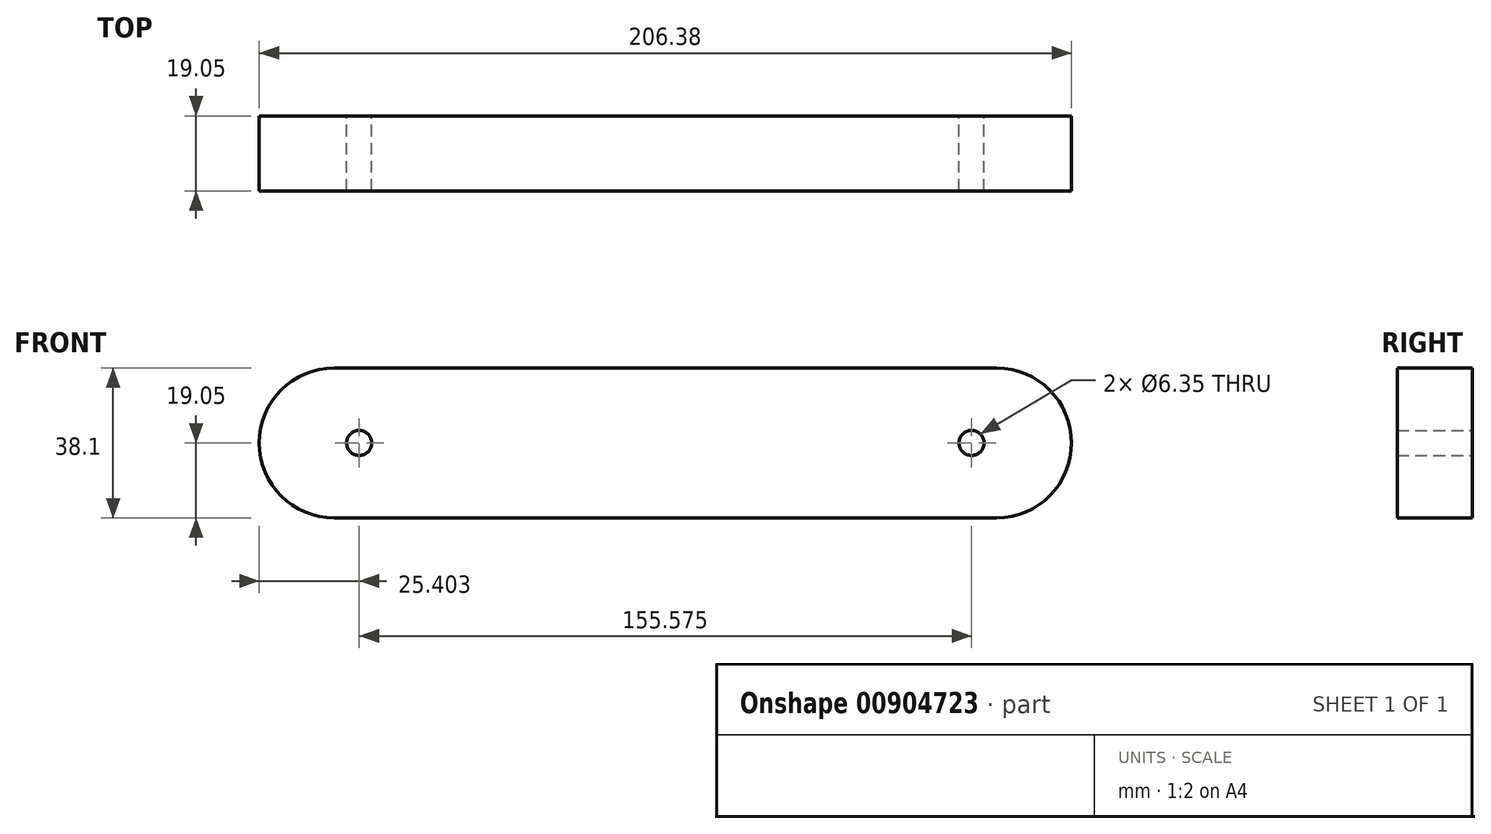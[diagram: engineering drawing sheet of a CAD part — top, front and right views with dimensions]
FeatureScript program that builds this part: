
annotation { "Feature Type Name" : "Feature", "Feature Type Description" : "" }
export const myFeature = defineFeature(function(context is Context, id is Id, definition is map)
    precondition{}
    {
        {
            var Q0;
            Q0=qCreatedBy(makeId("Front.planeOp"),FACE);
            var sketch = newSketch(context, id + "F0", { "sketchPlane" : qUnion([Q0])});
            skLineSegment(sketch, "E0.bottom", {"start": v(-84.14, -19.05) * mm, "end": v(84.14, -19.05) * mm});
            skLineSegment(sketch, "E0.top", {"start": v(-84.14, 19.05) * mm, "end": v(84.14, 19.05) * mm});
            skPoint(sketch, "E0.middle", {"position": v(0, 0) * mm});
            skArc(sketch, "E1", {"start": v(-84.14, 19.05) * mm, "mid": v(-103.19, 0) * mm, "end": v(-84.14, -19.05) * mm});
            skArc(sketch, "E2", {"start": v(84.14, 19.05) * mm, "mid": v(103.19, 0) * mm, "end": v(84.14, -19.05) * mm});
            skPoint(sketch, "E3", {"position": v(-77.79, 0) * mm});
            skCircle(sketch, "E4", {"center": v(-77.79, 0) * mm, "radius": 3.18 * mm});
            skCircle(sketch, "E5.MirrorC", {"center": v(77.79, 0) * mm, "radius": 3.18 * mm});
            skSolve(sketch);
        }
        {
            var Q0;
            Q0 = qSketchRegion(id + "F0", true);
            extrude(context, id + "F1", {"entities" : qUnion([Q0]), "depth" : 19.05 * mm, "offsetDistance" : 25.4 * mm});
        }
    });
